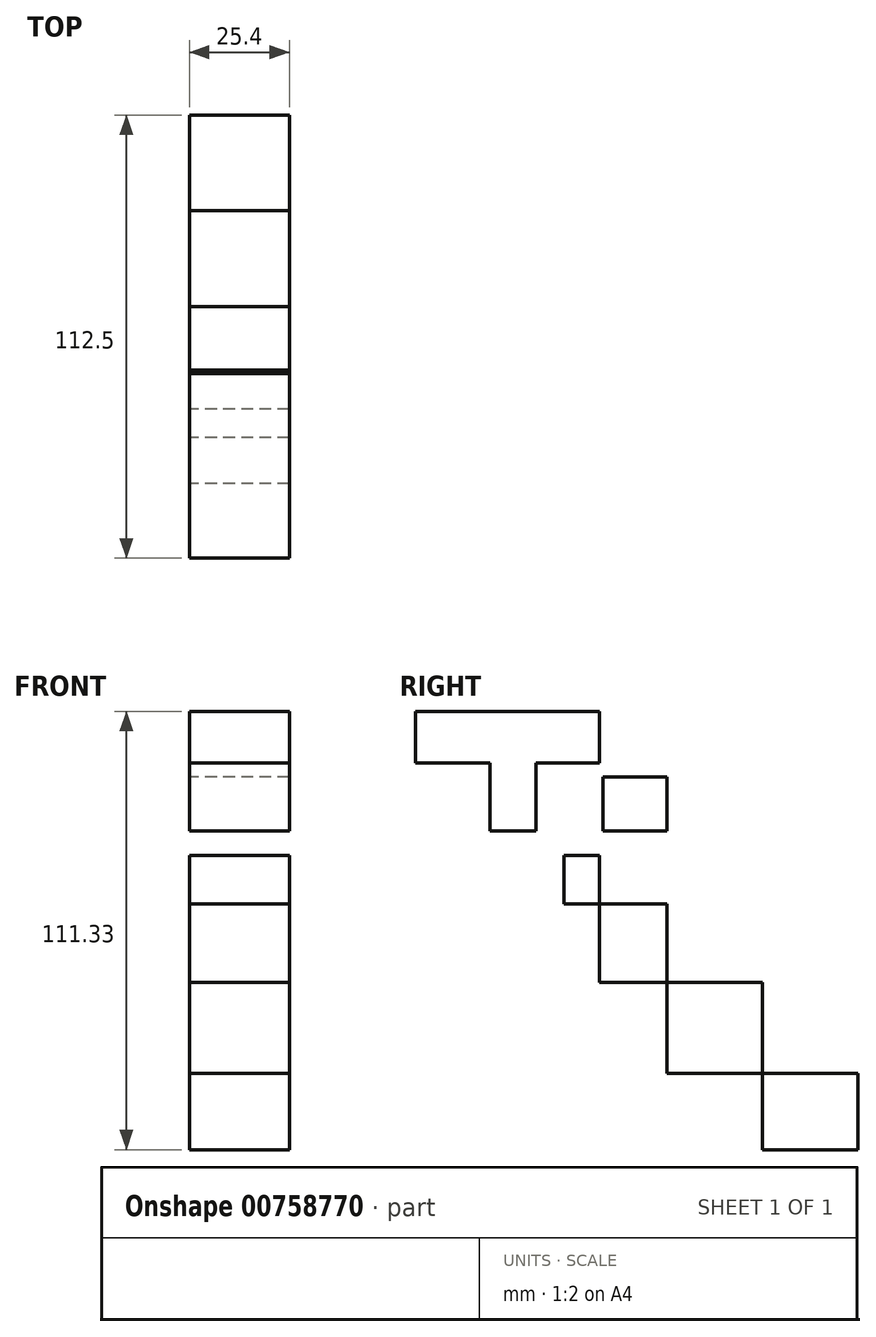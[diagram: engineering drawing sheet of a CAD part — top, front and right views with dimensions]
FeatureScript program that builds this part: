
annotation { "Feature Type Name" : "Feature", "Feature Type Description" : "" }
export const myFeature = defineFeature(function(context is Context, id is Id, definition is map)
    precondition{}
    {
        {
            var Q0;
            Q0=qCreatedBy(makeId("Right.planeOp"),FACE);
            var sketch = newSketch(context, id + "F0", { "sketchPlane" : qUnion([Q0])});
            skLineSegment(sketch, "E0.bottom", {"start": v(-441, 245.43) * mm, "end": v(-422.08, 245.43) * mm});
            skLineSegment(sketch, "E0.top", {"start": v(-441, 232.33) * mm, "end": v(-422.08, 232.33) * mm});
            skLineSegment(sketch, "E0.left", {"start": v(-441, 245.43) * mm, "end": v(-441, 232.33) * mm});
            skLineSegment(sketch, "E0.right", {"start": v(-422.08, 245.43) * mm, "end": v(-422.08, 232.33) * mm});
            skLineSegment(sketch, "E1.bottom", {"start": v(-422.08, 232.33) * mm, "end": v(-410.38, 232.33) * mm});
            skLineSegment(sketch, "E1.top", {"start": v(-422.08, 215.05) * mm, "end": v(-410.38, 215.05) * mm});
            skLineSegment(sketch, "E1.left", {"start": v(-422.08, 232.33) * mm, "end": v(-422.08, 215.05) * mm});
            skLineSegment(sketch, "E1.right", {"start": v(-410.38, 232.33) * mm, "end": v(-410.38, 215.05) * mm});
            skLineSegment(sketch, "E2.bottom", {"start": v(-403.19, 208.85) * mm, "end": v(-394.19, 208.85) * mm});
            skLineSegment(sketch, "E2.top", {"start": v(-403.19, 196.56) * mm, "end": v(-394.19, 196.56) * mm});
            skLineSegment(sketch, "E2.left", {"start": v(-403.19, 208.85) * mm, "end": v(-403.19, 196.56) * mm});
            skLineSegment(sketch, "E2.right", {"start": v(-394.19, 208.85) * mm, "end": v(-394.19, 196.56) * mm});
            skLineSegment(sketch, "E3.bottom", {"start": v(-394.19, 196.56) * mm, "end": v(-377.09, 196.56) * mm});
            skLineSegment(sketch, "E3.top", {"start": v(-394.19, 176.58) * mm, "end": v(-377.09, 176.58) * mm});
            skLineSegment(sketch, "E3.left", {"start": v(-394.19, 196.56) * mm, "end": v(-394.19, 176.58) * mm});
            skLineSegment(sketch, "E3.right", {"start": v(-377.09, 196.56) * mm, "end": v(-377.09, 176.58) * mm});
            skLineSegment(sketch, "E4.bottom", {"start": v(-377.09, 176.58) * mm, "end": v(-352.8, 176.58) * mm});
            skLineSegment(sketch, "E4.top", {"start": v(-377.09, 153.52) * mm, "end": v(-352.8, 153.52) * mm});
            skLineSegment(sketch, "E4.left", {"start": v(-377.09, 176.58) * mm, "end": v(-377.09, 153.52) * mm});
            skLineSegment(sketch, "E4.right", {"start": v(-352.8, 176.58) * mm, "end": v(-352.8, 153.52) * mm});
            skLineSegment(sketch, "E5.bottom", {"start": v(-352.8, 153.52) * mm, "end": v(-328.5, 153.52) * mm});
            skLineSegment(sketch, "E5.top", {"start": v(-352.8, 134.1) * mm, "end": v(-328.5, 134.1) * mm});
            skLineSegment(sketch, "E5.left", {"start": v(-352.8, 153.52) * mm, "end": v(-352.8, 134.1) * mm});
            skLineSegment(sketch, "E5.right", {"start": v(-328.5, 153.52) * mm, "end": v(-328.5, 134.1) * mm});
            skLineSegment(sketch, "E6.bottom", {"start": v(-422.08, 245.43) * mm, "end": v(-394.19, 245.43) * mm});
            skLineSegment(sketch, "E6.top", {"start": v(-422.08, 232.33) * mm, "end": v(-394.19, 232.33) * mm});
            skLineSegment(sketch, "E6.right", {"start": v(-394.19, 245.43) * mm, "end": v(-394.19, 232.33) * mm});
            skLineSegment(sketch, "E7.bottom", {"start": v(-393.29, 228.84) * mm, "end": v(-377.09, 228.84) * mm});
            skLineSegment(sketch, "E7.top", {"start": v(-393.29, 215.05) * mm, "end": v(-377.09, 215.05) * mm});
            skLineSegment(sketch, "E7.left", {"start": v(-393.29, 228.84) * mm, "end": v(-393.29, 215.05) * mm});
            skLineSegment(sketch, "E7.right", {"start": v(-377.09, 228.84) * mm, "end": v(-377.09, 215.05) * mm});
            skSolve(sketch);
        }
        {
            var Q0;
            Q0 = qSketchRegion(id + "F0", true);
            extrude(context, id + "F1", {"entities" : qUnion([Q0]), "depth" : 25.4 * mm, "offsetDistance" : 25.4 * mm});
        }
    });
